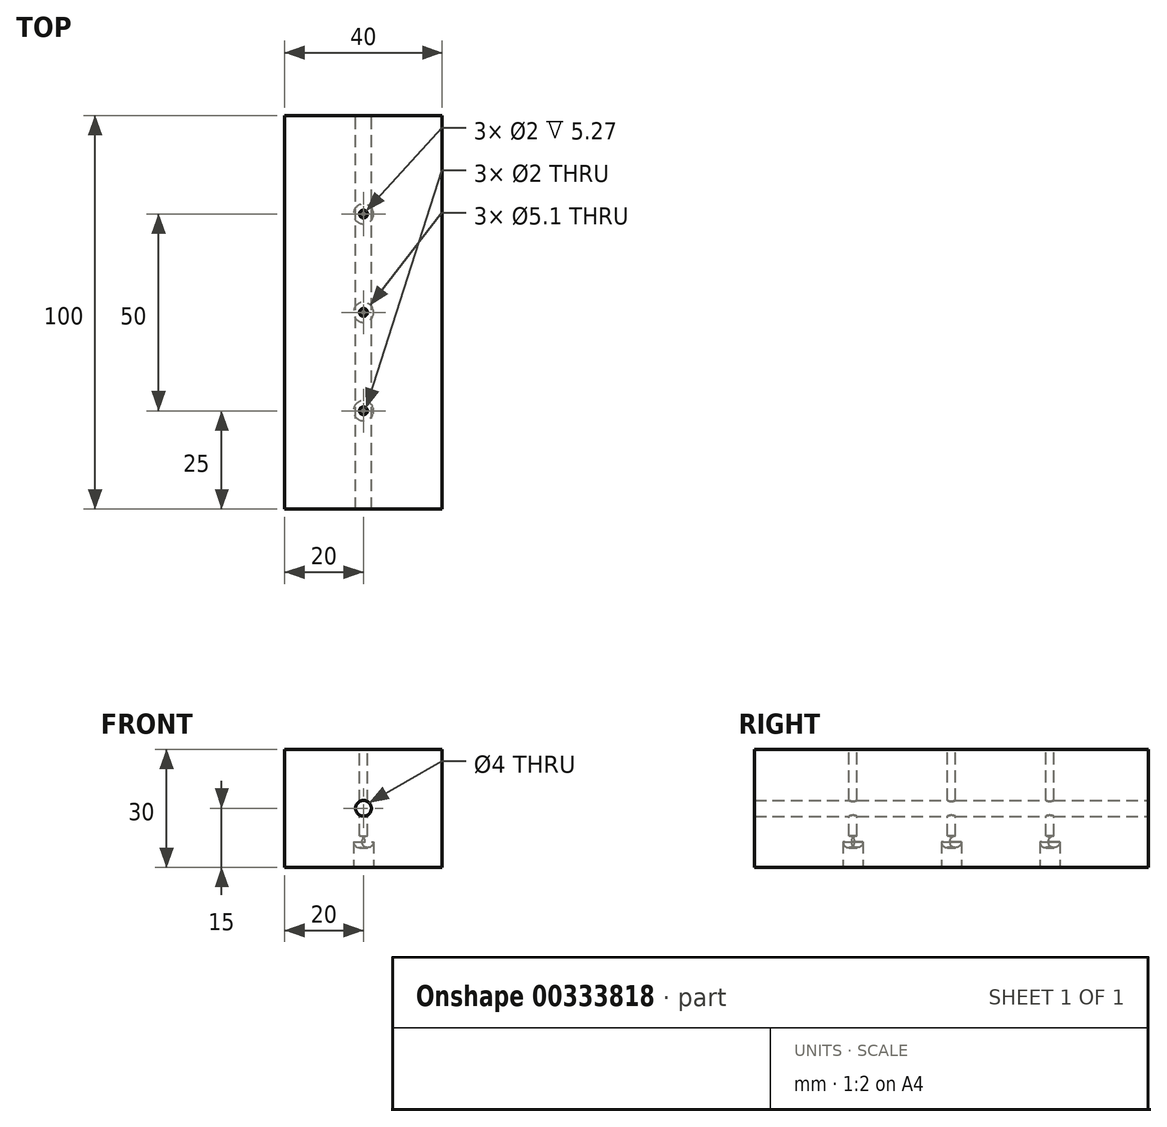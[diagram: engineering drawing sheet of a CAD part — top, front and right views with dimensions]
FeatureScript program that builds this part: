
annotation { "Feature Type Name" : "Feature", "Feature Type Description" : "" }
export const myFeature = defineFeature(function(context is Context, id is Id, definition is map)
    precondition{}
    {
        {
            var Q0;
            Q0=qCreatedBy(makeId("Front.planeOp"),FACE);
            var sketch = newSketch(context, id + "F0", { "sketchPlane" : qUnion([Q0])});
            skLineSegment(sketch, "E0.bottom", {"start": v(20, 15) * mm, "end": v(-20, 15) * mm});
            skLineSegment(sketch, "E0.top", {"start": v(20, -15) * mm, "end": v(-20, -15) * mm});
            skLineSegment(sketch, "E0.left", {"start": v(20, 15) * mm, "end": v(20, -15) * mm});
            skLineSegment(sketch, "E0.right", {"start": v(-20, 15) * mm, "end": v(-20, -15) * mm});
            skPoint(sketch, "E0.middle", {"position": v(0, 0) * mm});
            skCircle(sketch, "E1", {"center": v(0, 0) * mm, "radius": 2 * mm});
            skSolve(sketch);
        }
        {
            var Q0;
            Q0=makeQuery(id+"F0.imprint","IMPRINT",FACE,{"disambiguationData":[TD([[makeQuery(id+"F0.imprint","IMPRINT",EDGE,{"derivedFrom":sQuery(id+"F0.wireOp",EDGE,"E0.bottom")}),1.0]])]});
            extrude(context, id + "F1", {"entities" : qUnion([Q0]), "depth" : 100 * mm});
        }
        {
            var Q0;
            Q0=makeQuery(id+"F1.opExtrude","SWEPT_FACE",FACE,{"disambiguationData":[OSD([sQuery(id+"F0.wireOp",EDGE,"E0.bottom")])]});
            var sketch = newSketch(context, id + "F2", { "sketchPlane" : qUnion([Q0])});
            skCircle(sketch, "E2", {"center": v(0, -25) * mm, "radius": 1 * mm});
            skCircle(sketch, "E3", {"center": v(0, -50) * mm, "radius": 1 * mm});
            skCircle(sketch, "E4", {"center": v(0, -75) * mm, "radius": 1 * mm});
            skSolve(sketch);
        }
        {
            var Q0;
            Q0 = qSketchRegion(id + "F2", true);
            extrude(context, id + "F3", {"entities" : qUnion([Q0]), "operationType" : NewBodyOperationType.REMOVE, "oppositeDirection" : true, "depth" : 30 * mm});
        }
        {
            var Q0;
            Q0=makeQuery(id+"F1.opExtrude","SWEPT_FACE",FACE,{"disambiguationData":[OSD([sQuery(id+"F0.wireOp",EDGE,"E0.top")])]});
            var sketch = newSketch(context, id + "F4", { "sketchPlane" : qUnion([Q0])});
            skCircle(sketch, "E5", {"center": v(0, 25) * mm, "radius": 2.55 * mm});
            skCircle(sketch, "E6", {"center": v(0, 50) * mm, "radius": 2.55 * mm});
            skCircle(sketch, "E7", {"center": v(0, 75) * mm, "radius": 2.55 * mm});
            skSolve(sketch);
        }
        {
            var Q0;
            Q0 = qSketchRegion(id + "F4", true);
            extrude(context, id + "F5", {"entities" : qUnion([Q0]), "operationType" : NewBodyOperationType.REMOVE, "oppositeDirection" : true, "depth" : 8 * mm});
        }
        {
            var Q0;
            Q0=makeQuery(id+"F5.boolean.opBoolean","COPY",EDGE,{"derivedFrom":makeQuery(id+"F5.opExtrude","CAP_EDGE",EDGE,{"disambiguationData":[OSD([sQuery(id+"F4.wireOp",EDGE,"E5")])],"isStart":false})});
            fillet(context, id + "F6", {"entities" : qUnion([Q0]), "radius" : 1.5 * mm, "tangentPropagation" : true, "allowEdgeOverflow" : false});
        }
        {
            var Q0;
            Q0=makeQuery(id+"F5.boolean.opBoolean","COPY",EDGE,{"derivedFrom":makeQuery(id+"F5.opExtrude","CAP_EDGE",EDGE,{"disambiguationData":[OSD([sQuery(id+"F4.wireOp",EDGE,"E6")])],"isStart":false})});
            fillet(context, id + "F7", {"entities" : qUnion([Q0]), "radius" : 1.5 * mm, "tangentPropagation" : true, "allowEdgeOverflow" : false});
        }
        {
            var Q0;
            Q0=makeQuery(id+"F5.boolean.opBoolean","COPY",EDGE,{"derivedFrom":makeQuery(id+"F5.opExtrude","CAP_EDGE",EDGE,{"disambiguationData":[OSD([sQuery(id+"F4.wireOp",EDGE,"E7")])],"isStart":false})});
            fillet(context, id + "F8", {"entities" : qUnion([Q0]), "radius" : 1.5 * mm, "tangentPropagation" : true, "allowEdgeOverflow" : false});
        }
    });
